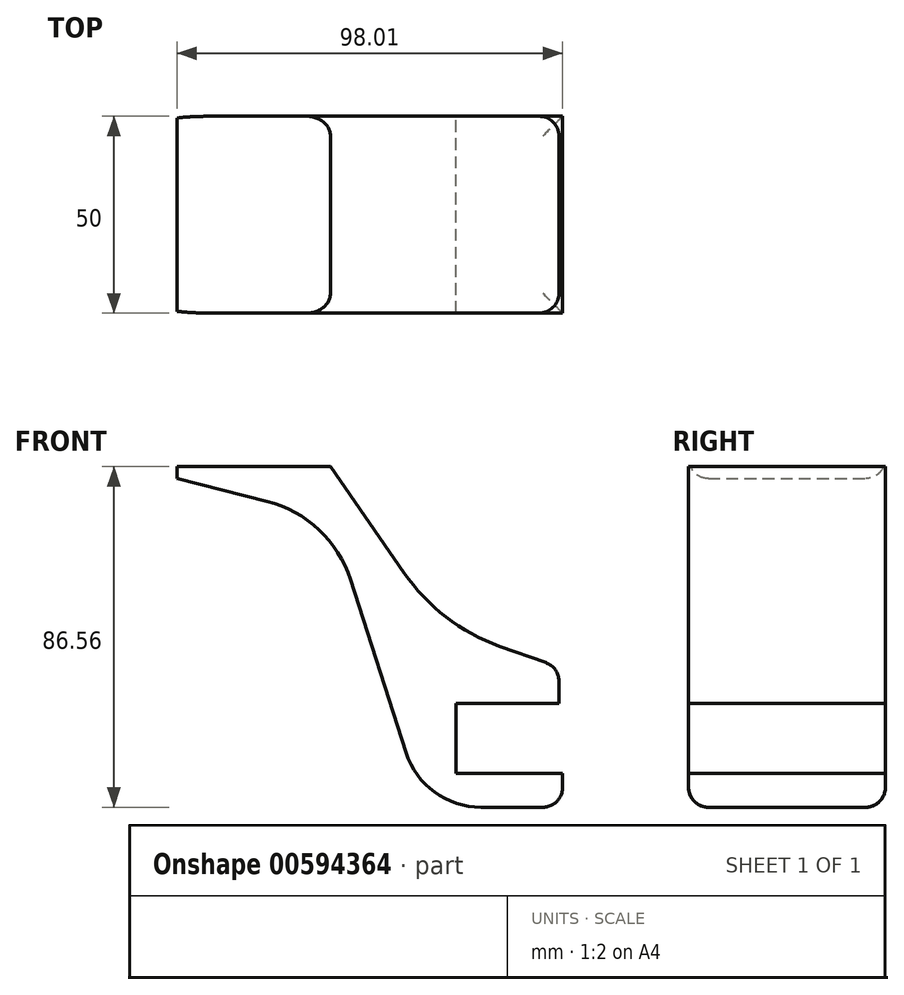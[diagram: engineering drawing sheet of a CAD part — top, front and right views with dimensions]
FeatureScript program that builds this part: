
annotation { "Feature Type Name" : "Feature", "Feature Type Description" : "" }
export const myFeature = defineFeature(function(context is Context, id is Id, definition is map)
    precondition{}
    {
        {
            var Q0;
            Q0=qCreatedBy(makeId("Front.planeOp"),FACE);
            var sketch = newSketch(context, id + "F0", { "sketchPlane" : qUnion([Q0])});
            skLineSegment(sketch, "E0", {"start": v(0, -41.9) * mm, "end": v(35.3, -41.9) * mm});
            skLineSegment(sketch, "E1", {"start": v(35.3, -41.9) * mm, "end": v(35.3, -33.28) * mm});
            skLineSegment(sketch, "E2", {"start": v(35.3, -33.28) * mm, "end": v(8.23, -33.28) * mm});
            skLineSegment(sketch, "E3", {"start": v(8.23, -33.28) * mm, "end": v(8.23, -15.56) * mm});
            skLineSegment(sketch, "E4", {"start": v(8.23, -15.56) * mm, "end": v(34.36, -15.56) * mm});
            skLineSegment(sketch, "E5", {"start": v(34.36, -15.56) * mm, "end": v(34.36, -6.34) * mm});
            skLineSegment(sketch, "E6", {"start": v(-23.66, 44.67) * mm, "end": v(-62.7, 44.67) * mm});
            skLineSegment(sketch, "E7", {"start": v(0, -41.9) * mm, "end": v(-23.66, 31.75) * mm});
            skLineSegment(sketch, "E8", {"start": v(-23.66, 31.75) * mm, "end": v(-62.7, 41.63) * mm});
            skLineSegment(sketch, "E9", {"start": v(-62.7, 41.63) * mm, "end": v(-62.7, 44.67) * mm});
            skLineSegment(sketch, "E10", {"start": v(4.18, 4.43) * mm, "end": v(34.36, -6.34) * mm});
            skLineSegment(sketch, "E11", {"start": v(4.18, 4.43) * mm, "end": v(-23.66, 44.67) * mm});
            skSolve(sketch);
        }
        {
            var Q0;
            Q0 = qSketchRegion(id + "F0", true);
            extrude(context, id + "F1", {"entities" : qUnion([Q0]), "depth" : 50 * mm, "offsetDistance" : 25 * mm});
        }
        {
            var Q0;
            Q0=makeQuery(id+"F1.opExtrude","SWEPT_EDGE",EDGE,{"disambiguationData":[OSD([sQuery(id+"F0.wireOp",EDGE,"E10"),sQuery(id+"F0.wireOp",EDGE,"E11")])]});
            fillet(context, id + "F2", {"entities" : qUnion([Q0]), "radius" : 50 * mm, "tangentPropagation" : true, "allowEdgeOverflow" : false});
        }
        {
            var Q0;
            Q0=makeQuery(id+"F1.opExtrude","SWEPT_EDGE",EDGE,{"disambiguationData":[OSD([sQuery(id+"F0.wireOp",EDGE,"E7"),sQuery(id+"F0.wireOp",EDGE,"E8")])]});
            fillet(context, id + "F3", {"entities" : qUnion([Q0]), "radius" : 30 * mm, "tangentPropagation" : true, "allowEdgeOverflow" : false});
        }
        {
            var Q0;
            Q0=makeQuery(id+"F1.opExtrude","SWEPT_EDGE",EDGE,{"disambiguationData":[OSD([sQuery(id+"F0.wireOp",EDGE,"E0"),sQuery(id+"F0.wireOp",EDGE,"E7")])]});
            fillet(context, id + "F4", {"entities" : qUnion([Q0]), "radius" : 20 * mm, "tangentPropagation" : true, "allowEdgeOverflow" : false});
        }
        {
            var Q0;
            Q0=makeQuery(id+"F1.opExtrude","SWEPT_EDGE",EDGE,{"disambiguationData":[OSD([sQuery(id+"F0.wireOp",EDGE,"E0"),sQuery(id+"F0.wireOp",EDGE,"E1")])]});
            var Q1;
            Q1=makeQuery(id+"F1.opExtrude","SWEPT_EDGE",EDGE,{"disambiguationData":[OSD([sQuery(id+"F0.wireOp",EDGE,"E5"),sQuery(id+"F0.wireOp",EDGE,"E10")])]});
            var Q2;
            Q2=makeQuery(id+"F4.opFillet","BLEND_FACE",FACE,{"disambiguationData":[OSD([sQuery(id+"F0.wireOp",EDGE,"E0"),sQuery(id+"F0.wireOp",EDGE,"E7")])]});
            fillet(context, id + "F5", {"entities" : qUnion([Q0, Q1, Q2]), "radius" : 5 * mm, "tangentPropagation" : true, "allowEdgeOverflow" : false});
        }
        {
            var Q0;
            Q0=makeQuery(id+"F1.opExtrude","CAP_EDGE",EDGE,{"disambiguationData":[OSD([sQuery(id+"F0.wireOp",EDGE,"E11")])],"isStart":false});
            var Q1;
            {var subQ0=sQuery(id+"F0.wireOp",EDGE,"E11");var subQ1=sQuery(id+"F0.wireOp",EDGE,"E10");Q1=makeQuery(id+"F2.opFillet","BLEND_EDGE",EDGE,{"blendedFrom":[makeQuery(id+"F1.opExtrude","SWEPT_EDGE",EDGE,{"disambiguationData":[OSD([subQ1,subQ0])]}),makeQuery(id+"F1.opExtrude","CAP_FACE",FACE,{"disambiguationData":[OSD([sQuery(id+"F0.wireOp",EDGE,"E0"),sQuery(id+"F0.wireOp",EDGE,"E1"),sQuery(id+"F0.wireOp",EDGE,"E2"),sQuery(id+"F0.wireOp",EDGE,"E3"),sQuery(id+"F0.wireOp",EDGE,"E4"),sQuery(id+"F0.wireOp",EDGE,"E5"),sQuery(id+"F0.wireOp",EDGE,"E6"),sQuery(id+"F0.wireOp",EDGE,"E7"),sQuery(id+"F0.wireOp",EDGE,"E8"),sQuery(id+"F0.wireOp",EDGE,"E9"),subQ1,subQ0])],"isStart":true})],"blendedInto":[makeQuery(id+"F1.opExtrude","CAP_FACE",FACE,{"disambiguationData":[OSD([sQuery(id+"F0.wireOp",EDGE,"E0"),sQuery(id+"F0.wireOp",EDGE,"E1"),sQuery(id+"F0.wireOp",EDGE,"E2"),sQuery(id+"F0.wireOp",EDGE,"E3"),sQuery(id+"F0.wireOp",EDGE,"E4"),sQuery(id+"F0.wireOp",EDGE,"E5"),sQuery(id+"F0.wireOp",EDGE,"E6"),sQuery(id+"F0.wireOp",EDGE,"E7"),sQuery(id+"F0.wireOp",EDGE,"E8"),sQuery(id+"F0.wireOp",EDGE,"E9"),subQ1,subQ0])],"isStart":true})]});}
            fillet(context, id + "F6", {"entities" : qUnion([Q0, Q1]), "radius" : 5 * mm, "tangentPropagation" : true, "allowEdgeOverflow" : false});
        }
    });
